# Revit family: BuzziWrap Front Desk
name_source: partatom
category: Furniture
revit_build: Autodesk Revit 2015 (Build: 20141119_0715(x64)
units: mm (PartAtom-declared; Revit-internal decimal feet)

## types (17) — shared parameters
BuzziWrap Desk Right Terminate 39.37x 27.56 = No
Middle Panel Length = 3' - 0"
Panel Material = <By Category>

## per-type parameters (varying)
- BuzziWrap Desk Full- 47.24 x 27.56: BuzziWrap Desk Center 39.37x 21.06=No; BuzziWrap Desk Center 39.37x 27.56=No; BuzziWrap Desk Center 43.31x 21.06=No; BuzziWrap Desk Center 43.31x 27.56=No; BuzziWrap Desk Center 47.24x 21.06=Yes; BuzziWrap Desk Center 47.24x 27.56=No; BuzziWrap Desk Left 39.37x 21.06=No; BuzziWrap Desk Left 39.37x 27.56=No; BuzziWrap Desk Left 43.31x 21.06=No; BuzziWrap Desk Left 43.31x 27.56=No; BuzziWrap Desk Left 47.24x 21.06=No; BuzziWrap Desk Left 47.24x 27.56=No; BuzziWrap Desk Left Terminate 39.37x 21.06=No; BuzziWrap Desk Left Terminate 39.37x 27.56=No; BuzziWrap Desk Left Terminate 43.31x 21.06=No; BuzziWrap Desk Left Terminate 43.31x 27.56=No; BuzziWrap Desk Left Terminate 47.24x 21.06=Yes; BuzziWrap Desk Left Terminate 47.24x 27.56=No; BuzziWrap Desk Right 39.37x 21.06=No; BuzziWrap Desk Right 39.37x 27.56=No; BuzziWrap Desk Right 43.31x 21.06=No; BuzziWrap Desk Right 43.31x 27.56=No; BuzziWrap Desk Right 47.24x 21.06=Yes; BuzziWrap Desk Right 47.24x 27.56=No; BuzziWrap Desk Right Terminate 39.37x 21.06=No; BuzziWrap Desk Right Terminate 43.31x 21.06=No; BuzziWrap Desk Right Terminate 43.31x 27.56=No; BuzziWrap Desk Right Terminate 47.24x 21.06=No; BuzziWrap Desk Right Terminate 47.24x 27.56=No
- BuzziWrap Desk Left- 47.24 x 27.56: BuzziWrap Desk Center 39.37x 21.06=No; BuzziWrap Desk Center 39.37x 27.56=No; BuzziWrap Desk Center 43.31x 21.06=No; BuzziWrap Desk Center 43.31x 27.56=No; BuzziWrap Desk Center 47.24x 21.06=No; BuzziWrap Desk Center 47.24x 27.56=Yes; BuzziWrap Desk Left 39.37x 21.06=No; BuzziWrap Desk Left 39.37x 27.56=No; BuzziWrap Desk Left 43.31x 21.06=No; BuzziWrap Desk Left 43.31x 27.56=No; BuzziWrap Desk Left 47.24x 21.06=No; BuzziWrap Desk Left 47.24x 27.56=Yes; BuzziWrap Desk Left Terminate 39.37x 21.06=No; BuzziWrap Desk Left Terminate 39.37x 27.56=No; BuzziWrap Desk Left Terminate 43.31x 21.06=No; BuzziWrap Desk Left Terminate 43.31x 27.56=No; BuzziWrap Desk Left Terminate 47.24x 21.06=No; BuzziWrap Desk Left Terminate 47.24x 27.56=No; BuzziWrap Desk Right 39.37x 21.06=No; BuzziWrap Desk Right 39.37x 27.56=No; BuzziWrap Desk Right 43.31x 21.06=No; BuzziWrap Desk Right 43.31x 27.56=No; BuzziWrap Desk Right 47.24x 21.06=No; BuzziWrap Desk Right 47.24x 27.56=No; BuzziWrap Desk Right Terminate 39.37x 21.06=No; BuzziWrap Desk Right Terminate 43.31x 21.06=No; BuzziWrap Desk Right Terminate 43.31x 27.56=No; BuzziWrap Desk Right Terminate 47.24x 21.06=No; BuzziWrap Desk Right Terminate 47.24x 27.56=Yes
- BuzziWrap Desk Right- 47.24 x 27.56: BuzziWrap Desk Center 39.37x 21.06=No; BuzziWrap Desk Center 39.37x 27.56=No; BuzziWrap Desk Center 43.31x 21.06=No; BuzziWrap Desk Center 43.31x 27.56=No; BuzziWrap Desk Center 47.24x 21.06=No; BuzziWrap Desk Center 47.24x 27.56=Yes; BuzziWrap Desk Left 39.37x 21.06=No; BuzziWrap Desk Left 39.37x 27.56=No; BuzziWrap Desk Left 43.31x 21.06=No; BuzziWrap Desk Left 43.31x 27.56=No; BuzziWrap Desk Left 47.24x 21.06=No; BuzziWrap Desk Left 47.24x 27.56=No; BuzziWrap Desk Left Terminate 39.37x 21.06=No; BuzziWrap Desk Left Terminate 39.37x 27.56=No; BuzziWrap Desk Left Terminate 43.31x 21.06=No; BuzziWrap Desk Left Terminate 43.31x 27.56=No; BuzziWrap Desk Left Terminate 47.24x 21.06=No; BuzziWrap Desk Left Terminate 47.24x 27.56=Yes; BuzziWrap Desk Right 39.37x 21.06=No; BuzziWrap Desk Right 39.37x 27.56=No; BuzziWrap Desk Right 43.31x 21.06=No; BuzziWrap Desk Right 43.31x 27.56=No; BuzziWrap Desk Right 47.24x 21.06=No; BuzziWrap Desk Right 47.24x 27.56=Yes; BuzziWrap Desk Right Terminate 39.37x 21.06=No; BuzziWrap Desk Right Terminate 43.31x 21.06=No; BuzziWrap Desk Right Terminate 43.31x 27.56=No; BuzziWrap Desk Right Terminate 47.24x 21.06=No; BuzziWrap Desk Right Terminate 47.24x 27.56=No
- BuzziWrap Desk Full- 47.24 x 21.06: BuzziWrap Desk Center 39.37x 21.06=No; BuzziWrap Desk Center 39.37x 27.56=No; BuzziWrap Desk Center 43.31x 21.06=No; BuzziWrap Desk Center 43.31x 27.56=No; BuzziWrap Desk Center 47.24x 21.06=Yes; BuzziWrap Desk Center 47.24x 27.56=No; BuzziWrap Desk Left 39.37x 21.06=No; BuzziWrap Desk Left 39.37x 27.56=No; BuzziWrap Desk Left 43.31x 21.06=No; BuzziWrap Desk Left 43.31x 27.56=No; BuzziWrap Desk Left 47.24x 21.06=Yes; BuzziWrap Desk Left 47.24x 27.56=No; BuzziWrap Desk Left Terminate 39.37x 21.06=No; BuzziWrap Desk Left Terminate 39.37x 27.56=No; BuzziWrap Desk Left Terminate 43.31x 21.06=No; BuzziWrap Desk Left Terminate 43.31x 27.56=No; BuzziWrap Desk Left Terminate 47.24x 21.06=No; BuzziWrap Desk Left Terminate 47.24x 27.56=No; BuzziWrap Desk Right 39.37x 21.06=No; BuzziWrap Desk Right 39.37x 27.56=No; BuzziWrap Desk Right 43.31x 21.06=No; BuzziWrap Desk Right 43.31x 27.56=No; BuzziWrap Desk Right 47.24x 21.06=Yes; BuzziWrap Desk Right 47.24x 27.56=No; BuzziWrap Desk Right Terminate 39.37x 21.06=No; BuzziWrap Desk Right Terminate 43.31x 21.06=No; BuzziWrap Desk Right Terminate 43.31x 27.56=No; BuzziWrap Desk Right Terminate 47.24x 21.06=No; BuzziWrap Desk Right Terminate 47.24x 27.56=No
- BuzziWrap Desk Left- 47.24 x 21.06: BuzziWrap Desk Center 39.37x 21.06=No; BuzziWrap Desk Center 39.37x 27.56=No; BuzziWrap Desk Center 43.31x 21.06=No; BuzziWrap Desk Center 43.31x 27.56=No; BuzziWrap Desk Center 47.24x 21.06=Yes; BuzziWrap Desk Center 47.24x 27.56=No; BuzziWrap Desk Left 39.37x 21.06=No; BuzziWrap Desk Left 39.37x 27.56=No; BuzziWrap Desk Left 43.31x 21.06=No; BuzziWrap Desk Left 43.31x 27.56=No; BuzziWrap Desk Left 47.24x 21.06=Yes; BuzziWrap Desk Left 47.24x 27.56=No; BuzziWrap Desk Left Terminate 39.37x 21.06=No; BuzziWrap Desk Left Terminate 39.37x 27.56=No; BuzziWrap Desk Left Terminate 43.31x 21.06=No; BuzziWrap Desk Left Terminate 43.31x 27.56=No; BuzziWrap Desk Left Terminate 47.24x 21.06=No; BuzziWrap Desk Left Terminate 47.24x 27.56=No; BuzziWrap Desk Right 39.37x 21.06=No; BuzziWrap Desk Right 39.37x 27.56=No; BuzziWrap Desk Right 43.31x 21.06=No; BuzziWrap Desk Right 43.31x 27.56=No; BuzziWrap Desk Right 47.24x 21.06=No; BuzziWrap Desk Right 47.24x 27.56=No; BuzziWrap Desk Right Terminate 39.37x 21.06=No; BuzziWrap Desk Right Terminate 43.31x 21.06=No; BuzziWrap Desk Right Terminate 43.31x 27.56=No; BuzziWrap Desk Right Terminate 47.24x 21.06=Yes; BuzziWrap Desk Right Terminate 47.24x 27.56=No
- BuzziWrap Desk Right- 47.24 x 21.06: BuzziWrap Desk Center 39.37x 21.06=No; BuzziWrap Desk Center 39.37x 27.56=No; BuzziWrap Desk Center 43.31x 21.06=No; BuzziWrap Desk Center 43.31x 27.56=No; BuzziWrap Desk Center 47.24x 21.06=Yes; BuzziWrap Desk Center 47.24x 27.56=No; BuzziWrap Desk Left 39.37x 21.06=No; BuzziWrap Desk Left 39.37x 27.56=No; BuzziWrap Desk Left 43.31x 21.06=No; BuzziWrap Desk Left 43.31x 27.56=No; BuzziWrap Desk Left 47.24x 21.06=No; BuzziWrap Desk Left 47.24x 27.56=No; BuzziWrap Desk Left Terminate 39.37x 21.06=No; BuzziWrap Desk Left Terminate 39.37x 27.56=No; BuzziWrap Desk Left Terminate 43.31x 21.06=No; BuzziWrap Desk Left Terminate 43.31x 27.56=No; BuzziWrap Desk Left Terminate 47.24x 21.06=Yes; BuzziWrap Desk Left Terminate 47.24x 27.56=No; BuzziWrap Desk Right 39.37x 21.06=No; BuzziWrap Desk Right 39.37x 27.56=No; BuzziWrap Desk Right 43.31x 21.06=No; BuzziWrap Desk Right 43.31x 27.56=No; BuzziWrap Desk Right 47.24x 21.06=Yes; BuzziWrap Desk Right 47.24x 27.56=No; BuzziWrap Desk Right Terminate 39.37x 21.06=No; BuzziWrap Desk Right Terminate 43.31x 21.06=No; BuzziWrap Desk Right Terminate 43.31x 27.56=No; BuzziWrap Desk Right Terminate 47.24x 21.06=No; BuzziWrap Desk Right Terminate 47.24x 27.56=No
- BuzziWrap desk Full- 43.31 x 27.56: BuzziWrap Desk Center 39.37x 21.06=No; BuzziWrap Desk Center 39.37x 27.56=No; BuzziWrap Desk Center 43.31x 21.06=No; BuzziWrap Desk Center 43.31x 27.56=Yes; BuzziWrap Desk Center 47.24x 21.06=No; BuzziWrap Desk Center 47.24x 27.56=No; BuzziWrap Desk Left 39.37x 21.06=No; BuzziWrap Desk Left 39.37x 27.56=No; BuzziWrap Desk Left 43.31x 21.06=No; BuzziWrap Desk Left 43.31x 27.56=Yes; BuzziWrap Desk Left 47.24x 21.06=No; BuzziWrap Desk Left 47.24x 27.56=No; BuzziWrap Desk Left Terminate 39.37x 21.06=No; BuzziWrap Desk Left Terminate 39.37x 27.56=No; BuzziWrap Desk Left Terminate 43.31x 21.06=No; BuzziWrap Desk Left Terminate 43.31x 27.56=No; BuzziWrap Desk Left Terminate 47.24x 21.06=No; BuzziWrap Desk Left Terminate 47.24x 27.56=No; BuzziWrap Desk Right 39.37x 21.06=No; BuzziWrap Desk Right 39.37x 27.56=No; BuzziWrap Desk Right 43.31x 21.06=No; BuzziWrap Desk Right 43.31x 27.56=Yes; BuzziWrap Desk Right 47.24x 21.06=No; BuzziWrap Desk Right 47.24x 27.56=No; BuzziWrap Desk Right Terminate 39.37x 21.06=No; BuzziWrap Desk Right Terminate 43.31x 21.06=No; BuzziWrap Desk Right Terminate 43.31x 27.56=No; BuzziWrap Desk Right Terminate 47.24x 21.06=No; BuzziWrap Desk Right Terminate 47.24x 27.56=No
- BuzziWrap Desk Left- 43.31 x 27.56: BuzziWrap Desk Center 39.37x 21.06=No; BuzziWrap Desk Center 39.37x 27.56=No; BuzziWrap Desk Center 43.31x 21.06=No; BuzziWrap Desk Center 43.31x 27.56=Yes; BuzziWrap Desk Center 47.24x 21.06=No; BuzziWrap Desk Center 47.24x 27.56=No; BuzziWrap Desk Left 39.37x 21.06=No; BuzziWrap Desk Left 39.37x 27.56=No; BuzziWrap Desk Left 43.31x 21.06=No; BuzziWrap Desk Left 43.31x 27.56=Yes; BuzziWrap Desk Left 47.24x 21.06=No; BuzziWrap Desk Left 47.24x 27.56=No; BuzziWrap Desk Left Terminate 39.37x 21.06=No; BuzziWrap Desk Left Terminate 39.37x 27.56=No; BuzziWrap Desk Left Terminate 43.31x 21.06=No; BuzziWrap Desk Left Terminate 43.31x 27.56=No; BuzziWrap Desk Left Terminate 47.24x 21.06=No; BuzziWrap Desk Left Terminate 47.24x 27.56=No; BuzziWrap Desk Right 39.37x 21.06=No; BuzziWrap Desk Right 39.37x 27.56=No; BuzziWrap Desk Right 43.31x 21.06=No; BuzziWrap Desk Right 43.31x 27.56=No; BuzziWrap Desk Right 47.24x 21.06=No; BuzziWrap Desk Right 47.24x 27.56=No; BuzziWrap Desk Right Terminate 39.37x 21.06=No; BuzziWrap Desk Right Terminate 43.31x 21.06=No; BuzziWrap Desk Right Terminate 43.31x 27.56=Yes; BuzziWrap Desk Right Terminate 47.24x 21.06=No; BuzziWrap Desk Right Terminate 47.24x 27.56=No
- BuzziWrap Desk Right 43.31 x 27.56: BuzziWrap Desk Center 39.37x 21.06=No; BuzziWrap Desk Center 39.37x 27.56=No; BuzziWrap Desk Center 43.31x 21.06=No; BuzziWrap Desk Center 43.31x 27.56=Yes; BuzziWrap Desk Center 47.24x 21.06=No; BuzziWrap Desk Center 47.24x 27.56=No; BuzziWrap Desk Left 39.37x 21.06=No; BuzziWrap Desk Left 39.37x 27.56=No; BuzziWrap Desk Left 43.31x 21.06=No; BuzziWrap Desk Left 43.31x 27.56=No; BuzziWrap Desk Left 47.24x 21.06=No; BuzziWrap Desk Left 47.24x 27.56=No; BuzziWrap Desk Left Terminate 39.37x 21.06=No; BuzziWrap Desk Left Terminate 39.37x 27.56=No; BuzziWrap Desk Left Terminate 43.31x 21.06=No; BuzziWrap Desk Left Terminate 43.31x 27.56=Yes; BuzziWrap Desk Left Terminate 47.24x 21.06=No; BuzziWrap Desk Left Terminate 47.24x 27.56=No; BuzziWrap Desk Right 39.37x 21.06=No; BuzziWrap Desk Right 39.37x 27.56=No; BuzziWrap Desk Right 43.31x 21.06=No; BuzziWrap Desk Right 43.31x 27.56=Yes; BuzziWrap Desk Right 47.24x 21.06=No; BuzziWrap Desk Right 47.24x 27.56=No; BuzziWrap Desk Right Terminate 39.37x 21.06=No; BuzziWrap Desk Right Terminate 43.31x 21.06=No; BuzziWrap Desk Right Terminate 43.31x 27.56=No; BuzziWrap Desk Right Terminate 47.24x 21.06=No; BuzziWrap Desk Right Terminate 47.24x 27.56=No
- BuzziWrap Desk Full 43.31 x 21.06: BuzziWrap Desk Center 39.37x 21.06=No; BuzziWrap Desk Center 39.37x 27.56=No; BuzziWrap Desk Center 43.31x 21.06=Yes; BuzziWrap Desk Center 43.31x 27.56=No; BuzziWrap Desk Center 47.24x 21.06=No; BuzziWrap Desk Center 47.24x 27.56=No; BuzziWrap Desk Left 39.37x 21.06=No; BuzziWrap Desk Left 39.37x 27.56=No; BuzziWrap Desk Left 43.31x 21.06=Yes; BuzziWrap Desk Left 43.31x 27.56=No; BuzziWrap Desk Left 47.24x 21.06=No; BuzziWrap Desk Left 47.24x 27.56=No; BuzziWrap Desk Left Terminate 39.37x 21.06=No; BuzziWrap Desk Left Terminate 39.37x 27.56=No; BuzziWrap Desk Left Terminate 43.31x 21.06=No; BuzziWrap Desk Left Terminate 43.31x 27.56=No; BuzziWrap Desk Left Terminate 47.24x 21.06=No; BuzziWrap Desk Left Terminate 47.24x 27.56=No; BuzziWrap Desk Right 39.37x 21.06=No; BuzziWrap Desk Right 39.37x 27.56=No; BuzziWrap Desk Right 43.31x 21.06=Yes; BuzziWrap Desk Right 43.31x 27.56=No; BuzziWrap Desk Right 47.24x 21.06=No; BuzziWrap Desk Right 47.24x 27.56=No; BuzziWrap Desk Right Terminate 39.37x 21.06=No; BuzziWrap Desk Right Terminate 43.31x 21.06=No; BuzziWrap Desk Right Terminate 43.31x 27.56=No; BuzziWrap Desk Right Terminate 47.24x 21.06=No; BuzziWrap Desk Right Terminate 47.24x 27.56=No
- BuzziWrap Desk Left 43.31 x 21.06: BuzziWrap Desk Center 39.37x 21.06=No; BuzziWrap Desk Center 39.37x 27.56=No; BuzziWrap Desk Center 43.31x 21.06=Yes; BuzziWrap Desk Center 43.31x 27.56=No; BuzziWrap Desk Center 47.24x 21.06=No; BuzziWrap Desk Center 47.24x 27.56=No; BuzziWrap Desk Left 39.37x 21.06=No; BuzziWrap Desk Left 39.37x 27.56=No; BuzziWrap Desk Left 43.31x 21.06=Yes; BuzziWrap Desk Left 43.31x 27.56=No; BuzziWrap Desk Left 47.24x 21.06=No; BuzziWrap Desk Left 47.24x 27.56=No; BuzziWrap Desk Left Terminate 39.37x 21.06=No; BuzziWrap Desk Left Terminate 39.37x 27.56=No; BuzziWrap Desk Left Terminate 43.31x 21.06=No; BuzziWrap Desk Left Terminate 43.31x 27.56=No; BuzziWrap Desk Left Terminate 47.24x 21.06=No; BuzziWrap Desk Left Terminate 47.24x 27.56=No; BuzziWrap Desk Right 39.37x 21.06=No; BuzziWrap Desk Right 39.37x 27.56=No; BuzziWrap Desk Right 43.31x 21.06=No; BuzziWrap Desk Right 43.31x 27.56=No; BuzziWrap Desk Right 47.24x 21.06=No; BuzziWrap Desk Right 47.24x 27.56=No; BuzziWrap Desk Right Terminate 39.37x 21.06=No; BuzziWrap Desk Right Terminate 43.31x 21.06=Yes; BuzziWrap Desk Right Terminate 43.31x 27.56=No; BuzziWrap Desk Right Terminate 47.24x 21.06=No; BuzziWrap Desk Right Terminate 47.24x 27.56=No
- BuzziWrap Desk Right 43.31 x 21.06: BuzziWrap Desk Center 39.37x 21.06=No; BuzziWrap Desk Center 39.37x 27.56=No; BuzziWrap Desk Center 43.31x 21.06=Yes; BuzziWrap Desk Center 43.31x 27.56=No; BuzziWrap Desk Center 47.24x 21.06=No; BuzziWrap Desk Center 47.24x 27.56=No; BuzziWrap Desk Left 39.37x 21.06=No; BuzziWrap Desk Left 39.37x 27.56=No; BuzziWrap Desk Left 43.31x 21.06=No; BuzziWrap Desk Left 43.31x 27.56=No; BuzziWrap Desk Left 47.24x 21.06=No; BuzziWrap Desk Left 47.24x 27.56=No; BuzziWrap Desk Left Terminate 39.37x 21.06=No; BuzziWrap Desk Left Terminate 39.37x 27.56=No; BuzziWrap Desk Left Terminate 43.31x 21.06=Yes; BuzziWrap Desk Left Terminate 43.31x 27.56=No; BuzziWrap Desk Left Terminate 47.24x 21.06=No; BuzziWrap Desk Left Terminate 47.24x 27.56=No; BuzziWrap Desk Right 39.37x 21.06=No; BuzziWrap Desk Right 39.37x 27.56=No; BuzziWrap Desk Right 43.31x 21.06=Yes; BuzziWrap Desk Right 43.31x 27.56=No; BuzziWrap Desk Right 47.24x 21.06=No; BuzziWrap Desk Right 47.24x 27.56=No; BuzziWrap Desk Right Terminate 39.37x 21.06=No; BuzziWrap Desk Right Terminate 43.31x 21.06=No; BuzziWrap Desk Right Terminate 43.31x 27.56=No; BuzziWrap Desk Right Terminate 47.24x 21.06=No; BuzziWrap Desk Right Terminate 47.24x 27.56=No
- BuzziWrap Desk Full 39.37 x 27.56: BuzziWrap Desk Center 39.37x 21.06=No; BuzziWrap Desk Center 39.37x 27.56=Yes; BuzziWrap Desk Center 43.31x 21.06=No; BuzziWrap Desk Center 43.31x 27.56=No; BuzziWrap Desk Center 47.24x 21.06=No; BuzziWrap Desk Center 47.24x 27.56=No; BuzziWrap Desk Left 39.37x 21.06=No; BuzziWrap Desk Left 39.37x 27.56=Yes; BuzziWrap Desk Left 43.31x 21.06=No; BuzziWrap Desk Left 43.31x 27.56=No; BuzziWrap Desk Left 47.24x 21.06=No; BuzziWrap Desk Left 47.24x 27.56=No; BuzziWrap Desk Left Terminate 39.37x 21.06=No; BuzziWrap Desk Left Terminate 39.37x 27.56=No; BuzziWrap Desk Left Terminate 43.31x 21.06=No; BuzziWrap Desk Left Terminate 43.31x 27.56=No; BuzziWrap Desk Left Terminate 47.24x 21.06=No; BuzziWrap Desk Left Terminate 47.24x 27.56=No; BuzziWrap Desk Right 39.37x 21.06=No; BuzziWrap Desk Right 39.37x 27.56=Yes; BuzziWrap Desk Right 43.31x 21.06=No; BuzziWrap Desk Right 43.31x 27.56=No; BuzziWrap Desk Right 47.24x 21.06=No; BuzziWrap Desk Right 47.24x 27.56=No; BuzziWrap Desk Right Terminate 39.37x 21.06=No; BuzziWrap Desk Right Terminate 43.31x 21.06=No; BuzziWrap Desk Right Terminate 43.31x 27.56=No; BuzziWrap Desk Right Terminate 47.24x 21.06=No; BuzziWrap Desk Right Terminate 47.24x 27.56=No
- BuzziWrap Desk Right 39.37 x 27.56: BuzziWrap Desk Center 39.37x 21.06=No; BuzziWrap Desk Center 39.37x 27.56=Yes; BuzziWrap Desk Center 43.31x 21.06=No; BuzziWrap Desk Center 43.31x 27.56=No; BuzziWrap Desk Center 47.24x 21.06=No; BuzziWrap Desk Center 47.24x 27.56=No; BuzziWrap Desk Left 39.37x 21.06=No; BuzziWrap Desk Left 39.37x 27.56=No; BuzziWrap Desk Left 43.31x 21.06=No; BuzziWrap Desk Left 43.31x 27.56=No; BuzziWrap Desk Left 47.24x 21.06=No; BuzziWrap Desk Left 47.24x 27.56=No; BuzziWrap Desk Left Terminate 39.37x 21.06=No; BuzziWrap Desk Left Terminate 39.37x 27.56=Yes; BuzziWrap Desk Left Terminate 43.31x 21.06=No; BuzziWrap Desk Left Terminate 43.31x 27.56=No; BuzziWrap Desk Left Terminate 47.24x 21.06=No; BuzziWrap Desk Left Terminate 47.24x 27.56=No; BuzziWrap Desk Right 39.37x 21.06=No; BuzziWrap Desk Right 39.37x 27.56=Yes; BuzziWrap Desk Right 43.31x 21.06=No; BuzziWrap Desk Right 43.31x 27.56=No; BuzziWrap Desk Right 47.24x 21.06=No; BuzziWrap Desk Right 47.24x 27.56=No; BuzziWrap Desk Right Terminate 39.37x 21.06=No; BuzziWrap Desk Right Terminate 43.31x 21.06=No; BuzziWrap Desk Right Terminate 43.31x 27.56=No; BuzziWrap Desk Right Terminate 47.24x 21.06=No; BuzziWrap Desk Right Terminate 47.24x 27.56=No
- BuzziWrap Desk Full 39.37 x 21.06: BuzziWrap Desk Center 39.37x 21.06=Yes; BuzziWrap Desk Center 39.37x 27.56=No; BuzziWrap Desk Center 43.31x 21.06=No; BuzziWrap Desk Center 43.31x 27.56=No; BuzziWrap Desk Center 47.24x 21.06=No; BuzziWrap Desk Center 47.24x 27.56=No; BuzziWrap Desk Left 39.37x 21.06=Yes; BuzziWrap Desk Left 39.37x 27.56=No; BuzziWrap Desk Left 43.31x 21.06=No; BuzziWrap Desk Left 43.31x 27.56=No; BuzziWrap Desk Left 47.24x 21.06=No; BuzziWrap Desk Left 47.24x 27.56=No; BuzziWrap Desk Left Terminate 39.37x 21.06=No; BuzziWrap Desk Left Terminate 39.37x 27.56=No; BuzziWrap Desk Left Terminate 43.31x 21.06=No; BuzziWrap Desk Left Terminate 43.31x 27.56=No; BuzziWrap Desk Left Terminate 47.24x 21.06=No; BuzziWrap Desk Left Terminate 47.24x 27.56=No; BuzziWrap Desk Right 39.37x 21.06=Yes; BuzziWrap Desk Right 39.37x 27.56=No; BuzziWrap Desk Right 43.31x 21.06=No; BuzziWrap Desk Right 43.31x 27.56=No; BuzziWrap Desk Right 47.24x 21.06=No; BuzziWrap Desk Right 47.24x 27.56=No; BuzziWrap Desk Right Terminate 39.37x 21.06=No; BuzziWrap Desk Right Terminate 43.31x 21.06=No; BuzziWrap Desk Right Terminate 43.31x 27.56=No; BuzziWrap Desk Right Terminate 47.24x 21.06=No; BuzziWrap Desk Right Terminate 47.24x 27.56=No
- BuzziWrap Desk Left 39.37 x 21.06: BuzziWrap Desk Center 39.37x 21.06=Yes; BuzziWrap Desk Center 39.37x 27.56=No; BuzziWrap Desk Center 43.31x 21.06=No; BuzziWrap Desk Center 43.31x 27.56=No; BuzziWrap Desk Center 47.24x 21.06=No; BuzziWrap Desk Center 47.24x 27.56=No; BuzziWrap Desk Left 39.37x 21.06=Yes; BuzziWrap Desk Left 39.37x 27.56=No; BuzziWrap Desk Left 43.31x 21.06=No; BuzziWrap Desk Left 43.31x 27.56=No; BuzziWrap Desk Left 47.24x 21.06=No; BuzziWrap Desk Left 47.24x 27.56=No; BuzziWrap Desk Left Terminate 39.37x 21.06=No; BuzziWrap Desk Left Terminate 39.37x 27.56=No; BuzziWrap Desk Left Terminate 43.31x 21.06=No; BuzziWrap Desk Left Terminate 43.31x 27.56=No; BuzziWrap Desk Left Terminate 47.24x 21.06=No; BuzziWrap Desk Left Terminate 47.24x 27.56=No; BuzziWrap Desk Right 39.37x 21.06=No; BuzziWrap Desk Right 39.37x 27.56=No; BuzziWrap Desk Right 43.31x 21.06=No; BuzziWrap Desk Right 43.31x 27.56=No; BuzziWrap Desk Right 47.24x 21.06=No; BuzziWrap Desk Right 47.24x 27.56=No; BuzziWrap Desk Right Terminate 39.37x 21.06=Yes; BuzziWrap Desk Right Terminate 43.31x 21.06=No; BuzziWrap Desk Right Terminate 43.31x 27.56=No; BuzziWrap Desk Right Terminate 47.24x 21.06=No; BuzziWrap Desk Right Terminate 47.24x 27.56=No
- BuzziWrap Desk Right 39.37 x 21.06: BuzziWrap Desk Center 39.37x 21.06=Yes; BuzziWrap Desk Center 39.37x 27.56=No; BuzziWrap Desk Center 43.31x 21.06=No; BuzziWrap Desk Center 43.31x 27.56=No; BuzziWrap Desk Center 47.24x 21.06=No; BuzziWrap Desk Center 47.24x 27.56=No; BuzziWrap Desk Left 39.37x 21.06=No; BuzziWrap Desk Left 39.37x 27.56=No; BuzziWrap Desk Left 43.31x 21.06=No; BuzziWrap Desk Left 43.31x 27.56=No; BuzziWrap Desk Left 47.24x 21.06=No; BuzziWrap Desk Left 47.24x 27.56=No; BuzziWrap Desk Left Terminate 39.37x 21.06=Yes; BuzziWrap Desk Left Terminate 39.37x 27.56=No; BuzziWrap Desk Left Terminate 43.31x 21.06=No; BuzziWrap Desk Left Terminate 43.31x 27.56=No; BuzziWrap Desk Left Terminate 47.24x 21.06=No; BuzziWrap Desk Left Terminate 47.24x 27.56=No; BuzziWrap Desk Right 39.37x 21.06=Yes; BuzziWrap Desk Right 39.37x 27.56=No; BuzziWrap Desk Right 43.31x 21.06=No; BuzziWrap Desk Right 43.31x 27.56=No; BuzziWrap Desk Right 47.24x 21.06=No; BuzziWrap Desk Right 47.24x 27.56=No; BuzziWrap Desk Right Terminate 39.37x 21.06=No; BuzziWrap Desk Right Terminate 43.31x 21.06=No; BuzziWrap Desk Right Terminate 43.31x 27.56=No; BuzziWrap Desk Right Terminate 47.24x 21.06=No; BuzziWrap Desk Right Terminate 47.24x 27.56=No

## geometry (parser evidence)
native form markers: Sweep x44
no freeform markers — native parametric forms only
